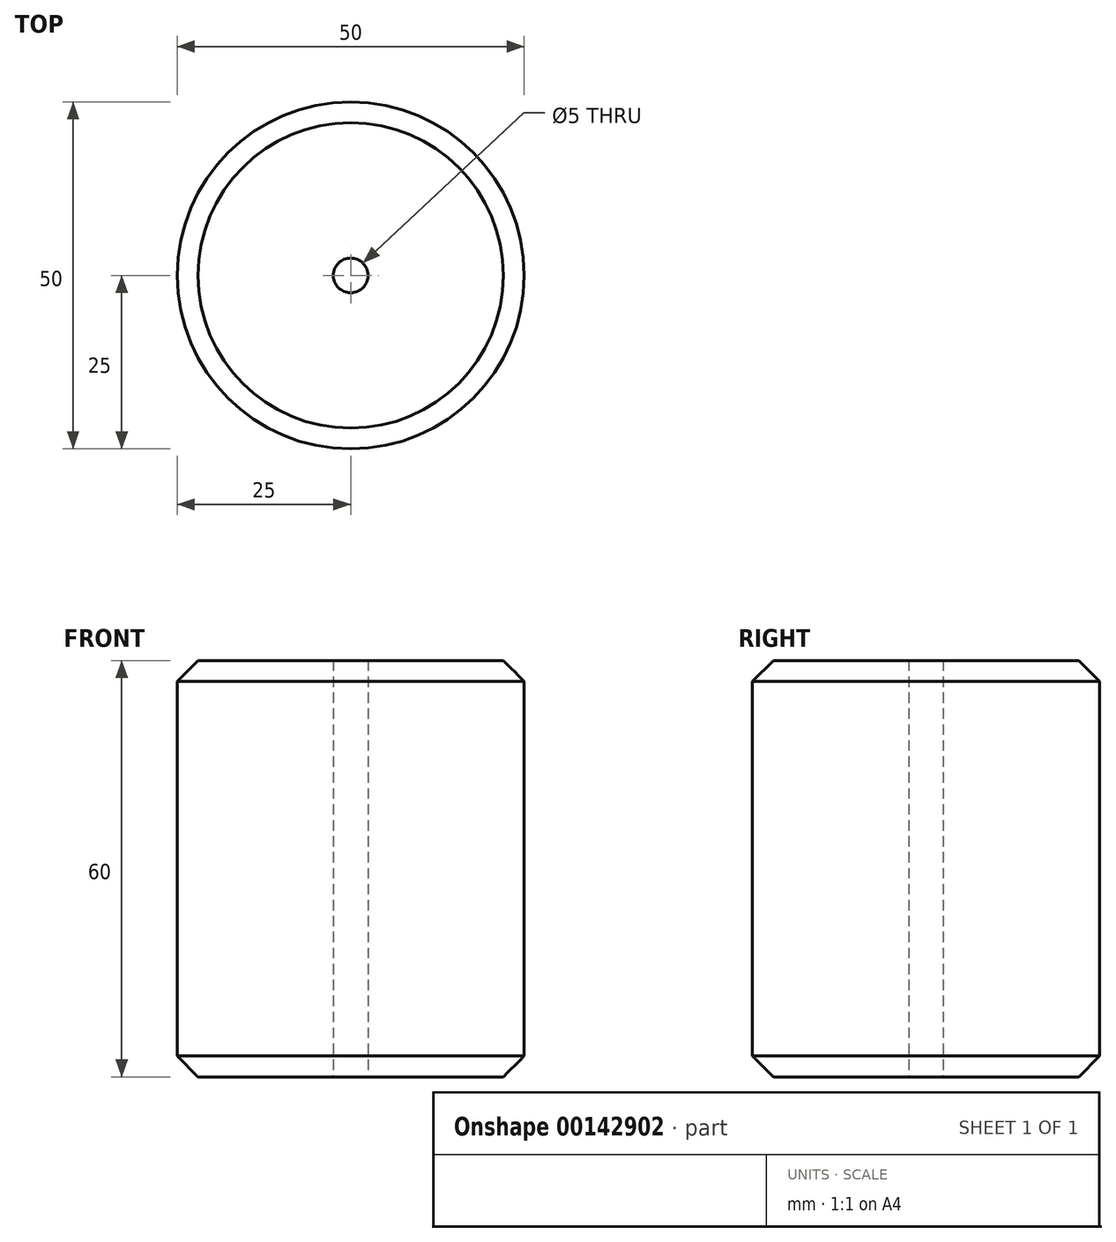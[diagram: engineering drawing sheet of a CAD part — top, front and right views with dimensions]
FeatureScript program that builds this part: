
annotation { "Feature Type Name" : "Feature", "Feature Type Description" : "" }
export const myFeature = defineFeature(function(context is Context, id is Id, definition is map)
    precondition{}
    {
        {
            var Q0;
            Q0=qCreatedBy(makeId("Top.planeOp"),FACE);
            var sketch = newSketch(context, id + "F0", { "sketchPlane" : qUnion([Q0])});
            skCircle(sketch, "E0", {"center": v(0, 0) * mm, "radius": 25 * mm});
            skCircle(sketch, "E1", {"center": v(0, 0) * mm, "radius": 2.5 * mm});
            skSolve(sketch);
        }
        {
            var Q0;
            Q0=makeQuery(id+"F0.imprint","IMPRINT",FACE,{"disambiguationData":[TD([[makeQuery(id+"F0.imprint","IMPRINT",EDGE,{"derivedFrom":sQuery(id+"F0.wireOp",EDGE,"E0")}),1.0]])]});
            var Q1;
            Q1=makeQuery(id+"F0.imprint","IMPRINT",FACE,{"disambiguationData":[TD([[makeQuery(id+"F0.imprint","IMPRINT",EDGE,{"derivedFrom":sQuery(id+"F0.wireOp",EDGE,"E1")}),1.0]])]});
            extrude(context, id + "F1", {"entities" : qUnion([Q0, Q1]), "depth" : 60 * mm});
        }
        {
            var Q0;
            Q0=makeQuery(id+"F0.imprint","IMPRINT",FACE,{"disambiguationData":[TD([[makeQuery(id+"F0.imprint","IMPRINT",EDGE,{"derivedFrom":sQuery(id+"F0.wireOp",EDGE,"E1")}),1.0]])]});
            extrude(context, id + "F2", {"entities" : qUnion([Q0]), "operationType" : NewBodyOperationType.REMOVE, "depth" : 60 * mm});
        }
        {
            var Q0;
            Q0=makeQuery(id+"F1.opExtrude","CAP_EDGE",EDGE,{"disambiguationData":[OSD([sQuery(id+"F0.wireOp",EDGE,"E0")])],"isStart":false});
            var Q1;
            Q1=makeQuery(id+"F1.opExtrude","CAP_EDGE",EDGE,{"disambiguationData":[OSD([sQuery(id+"F0.wireOp",EDGE,"E0")])],"isStart":true});
            chamfer(context, id + "F3", {"entities" : qUnion([Q0, Q1]), "width" : 3 * mm, "tangentPropagation" : true});
        }
    });
